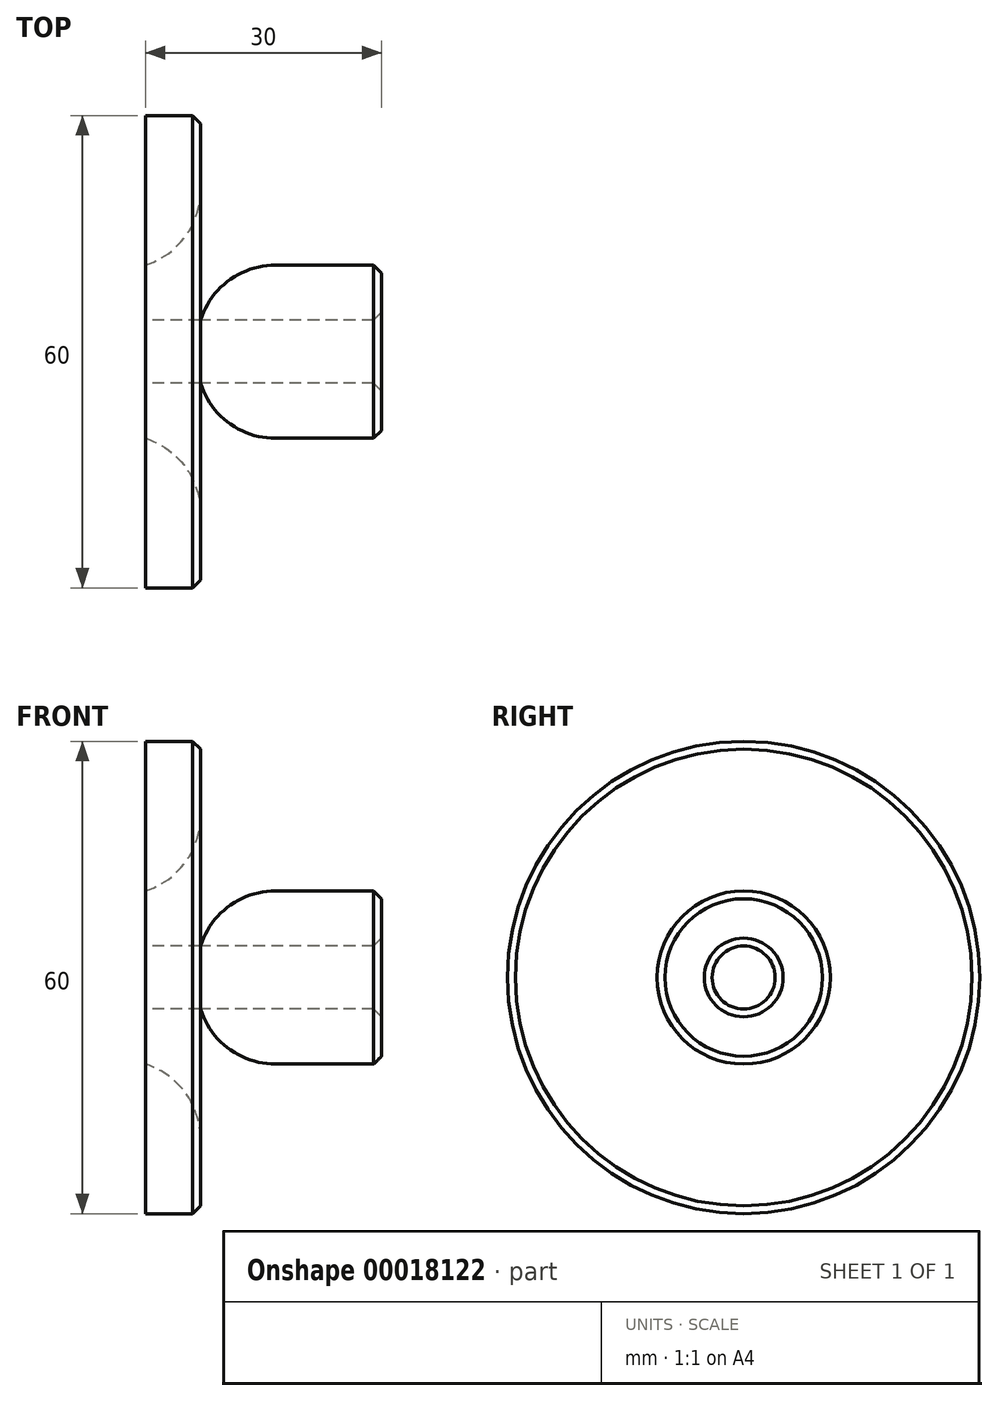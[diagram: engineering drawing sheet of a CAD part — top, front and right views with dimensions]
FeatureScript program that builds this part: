
annotation { "Feature Type Name" : "Feature", "Feature Type Description" : "" }
export const myFeature = defineFeature(function(context is Context, id is Id, definition is map)
    precondition{}
    {
        {
            var Q0;
            Q0=qCreatedBy(makeId("Front.planeOp"),FACE);
            var sketch = newSketch(context, id + "F0", { "sketchPlane" : qUnion([Q0])});
            skLineSegment(sketch, "E0", {"start": v(0, 0) * mm, "end": v(30, 0) * mm, "construction": true});
            skLineSegment(sketch, "E1.bottom", {"start": v(0, 30) * mm, "end": v(7, 30) * mm});
            skLineSegment(sketch, "E1.top", {"start": v(0, 0) * mm, "end": v(7, 0) * mm});
            skLineSegment(sketch, "E1.left", {"start": v(0, 30) * mm, "end": v(0, 0) * mm});
            skLineSegment(sketch, "E1.right", {"start": v(7, 30) * mm, "end": v(7, 0) * mm});
            skLineSegment(sketch, "E2.bottom", {"start": v(0, 11) * mm, "end": v(30, 11) * mm});
            skLineSegment(sketch, "E2.top", {"start": v(0, 4) * mm, "end": v(30, 4) * mm});
            skLineSegment(sketch, "E2.left", {"start": v(0, 11) * mm, "end": v(0, 4) * mm});
            skLineSegment(sketch, "E2.right", {"start": v(30, 11) * mm, "end": v(30, 4) * mm});
            skLineSegment(sketch, "E3.MirrorCS", {"start": v(0, -30) * mm, "end": v(0, 0) * mm});
            skLineSegment(sketch, "E4.MirrorCS", {"start": v(0, -4) * mm, "end": v(30, -4) * mm});
            skLineSegment(sketch, "E5.MirrorCS", {"start": v(0, -11) * mm, "end": v(0, -4) * mm});
            skLineSegment(sketch, "E6.MirrorCS", {"start": v(0, -30) * mm, "end": v(7, -30) * mm});
            skLineSegment(sketch, "E7.MirrorCS", {"start": v(30, -11) * mm, "end": v(30, -4) * mm});
            skLineSegment(sketch, "E8.MirrorCS", {"start": v(0, -11) * mm, "end": v(30, -11) * mm});
            skLineSegment(sketch, "E9.MirrorCS", {"start": v(7, -30) * mm, "end": v(7, 0) * mm});
            skSolve(sketch);
        }
        {
            var Q0;
            {var subQ5=sQuery(id+"F0.wireOp",EDGE,"E1.bottom");Q0=makeQuery(id+"F0.imprint","IMPRINT",FACE,{"disambiguationData":[TD([[makeQuery(id+"F0.imprint","IMPRINT",EDGE,{"derivedFrom":subQ5}),-1.0]])]});}
            var Q1;
            {var subQ0=sQuery(id+"F0.wireOp",EDGE,"E2.left");Q1=makeQuery(id+"F0.imprint","IMPRINT",FACE,{"disambiguationData":[TD([[makeQuery(id+"F0.imprint","IMPRINT",EDGE,{"derivedFrom":subQ0}),1.0]])]});}
            var Q2;
            {var subQ0=sQuery(id+"F0.wireOp",EDGE,"E2.right");Q2=makeQuery(id+"F0.imprint","IMPRINT",FACE,{"disambiguationData":[TD([[makeQuery(id+"F0.imprint","IMPRINT",EDGE,{"derivedFrom":subQ0}),-1.0]])]});}
            var Q3;
            {var subQ0=sQuery(id+"F0.wireOp",EDGE,"E1.top");Q3=makeQuery(id+"F0.imprint","IMPRINT",FACE,{"disambiguationData":[TD([[makeQuery(id+"F0.imprint","IMPRINT",EDGE,{"derivedFrom":subQ0}),1.0]])]});}
            var Q4;
            Q4=sQuery(id+"F0.wireOp",EDGE,"E0");
            revolve(context, id + "F1", {"entities" : qUnion([Q0, Q1, Q2, Q3]), "axis" : qUnion([Q4]), "revolveType" : RevolveType.FULL});
        }
        {
            var Q0;
            Q0=makeQuery(id+"F1.opRevolve","SWEPT_EDGE",EDGE,{"disambiguationData":[OSD([sQuery(id+"F0.wireOp",EDGE,"E1.right"),sQuery(id+"F0.wireOp",EDGE,"E2.bottom")])]});
            fillet(context, id + "F2", {"entities" : qUnion([Q0]), "radius" : 10 * mm, "tangentPropagation" : true, "allowEdgeOverflow" : false});
        }
        {
            var Q0;
            Q0=makeQuery(id+"F1.opRevolve","SWEPT_EDGE",EDGE,{"disambiguationData":[OSD([sQuery(id+"F0.wireOp",EDGE,"E2.bottom"),sQuery(id+"F0.wireOp",EDGE,"E2.right")])]});
            var Q1;
            Q1=makeQuery(id+"F1.opRevolve","SWEPT_EDGE",EDGE,{"disambiguationData":[OSD([sQuery(id+"F0.wireOp",EDGE,"E2.top"),sQuery(id+"F0.wireOp",EDGE,"E2.right")])]});
            chamfer(context, id + "F3", {"entities" : qUnion([Q0, Q1]), "width" : 1 * mm, "tangentPropagation" : true});
        }
        {
            var Q0;
            Q0=makeQuery(id+"F1.opRevolve","SWEPT_EDGE",EDGE,{"disambiguationData":[OSD([sQuery(id+"F0.wireOp",EDGE,"E1.bottom"),sQuery(id+"F0.wireOp",EDGE,"E1.right")])]});
            chamfer(context, id + "F4", {"entities" : qUnion([Q0]), "width" : 1 * mm, "tangentPropagation" : true});
        }
    });
